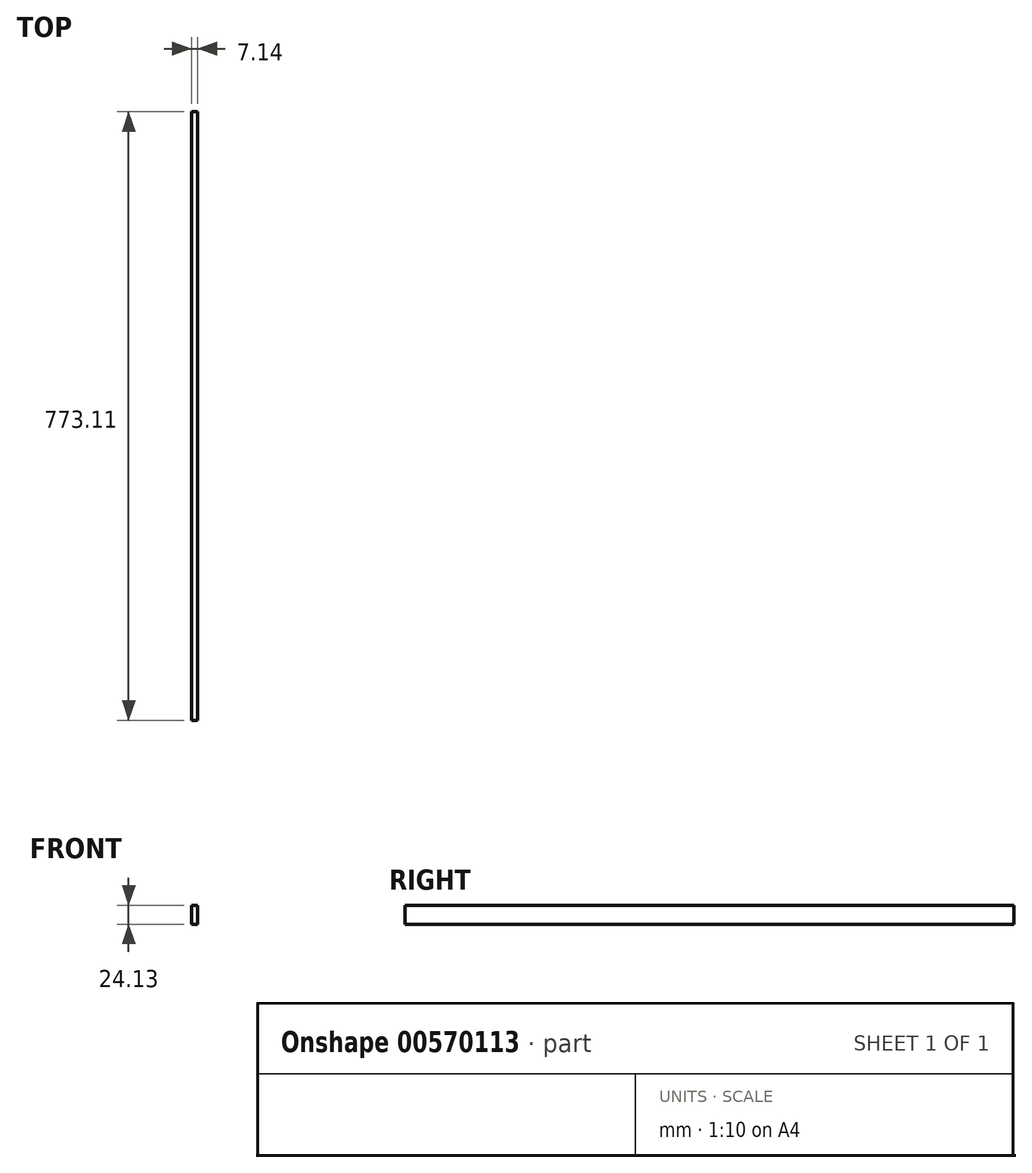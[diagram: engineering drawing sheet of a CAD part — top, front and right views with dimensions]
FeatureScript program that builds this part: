
annotation { "Feature Type Name" : "Feature", "Feature Type Description" : "" }
export const myFeature = defineFeature(function(context is Context, id is Id, definition is map)
    precondition{}
    {
        {
            var Q0;
            Q0=qCreatedBy(makeId("Front.planeOp"),FACE);
            var sketch = newSketch(context, id + "F0", { "sketchPlane" : qUnion([Q0])});
            skLineSegment(sketch, "E0.bottom", {"start": v(0, 0) * mm, "end": v(7.14, 0) * mm});
            skLineSegment(sketch, "E0.top", {"start": v(0, -24.13) * mm, "end": v(7.14, -24.13) * mm});
            skLineSegment(sketch, "E0.left", {"start": v(0, 0) * mm, "end": v(0, -24.13) * mm});
            skLineSegment(sketch, "E0.right", {"start": v(7.14, 0) * mm, "end": v(7.14, -24.13) * mm});
            skSolve(sketch);
        }
        {
            var Q0;
            Q0=makeQuery(id+"F0.imprint","IMPRINT",FACE,{"disambiguationData":[TD([[makeQuery(id+"F0.imprint","IMPRINT",EDGE,{"derivedFrom":sQuery(id+"F0.wireOp",EDGE,"E0.bottom")}),-1.0]])]});
            extrude(context, id + "F1", {"entities" : qUnion([Q0]), "depth" : 773.1 * mm, "offsetDistance" : 25.4 * mm});
        }
    });
